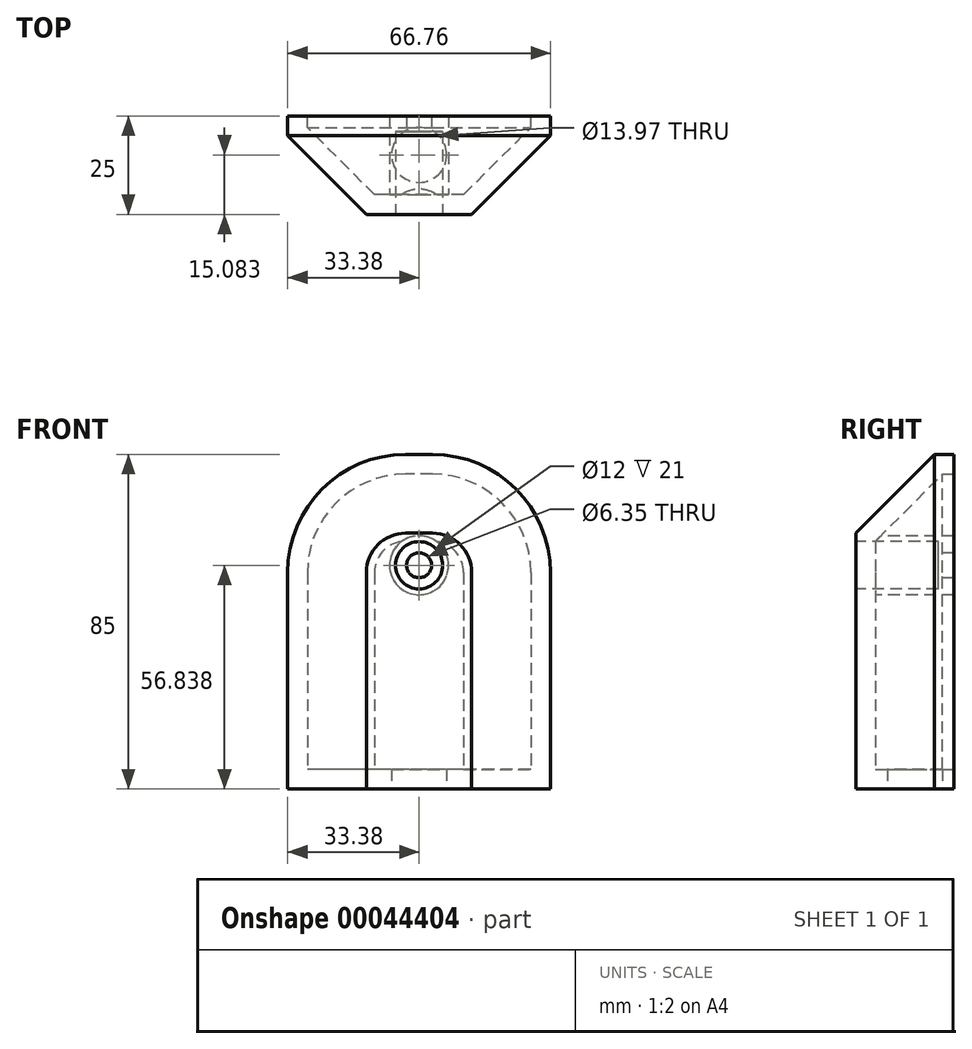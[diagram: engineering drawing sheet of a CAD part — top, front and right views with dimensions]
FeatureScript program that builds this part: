
annotation { "Feature Type Name" : "Feature", "Feature Type Description" : "" }
export const myFeature = defineFeature(function(context is Context, id is Id, definition is map)
    precondition{}
    {
        {
            var Q0;
            Q0=qCreatedBy(makeId("Front.planeOp"),FACE);
            var sketch = newSketch(context, id + "F0", { "sketchPlane" : qUnion([Q0])});
            skLineSegment(sketch, "E0.rect.bottom", {"start": v(3.38, 42.5) * mm, "end": v(-3.38, 42.5) * mm});
            skLineSegment(sketch, "E0.rect.top", {"start": v(33.38, -42.5) * mm, "end": v(-33.38, -42.5) * mm});
            skLineSegment(sketch, "E0.rect.left", {"start": v(33.38, 12.5) * mm, "end": v(33.38, -42.5) * mm});
            skLineSegment(sketch, "E0.rect.right", {"start": v(-33.38, 12.5) * mm, "end": v(-33.38, -42.5) * mm});
            skPoint(sketch, "E0.rect.middle", {"position": v(0, 0) * mm});
            skPoint(sketch, "E1.visualSharp", {"position": v(-33.38, 42.5) * mm});
            skArc(sketch, "E1.filletArc", {"start": v(-3.38, 42.5) * mm, "mid": v(-24.6, 33.71) * mm, "end": v(-33.38, 12.5) * mm});
            skPoint(sketch, "E2.visualSharp", {"position": v(33.38, 42.5) * mm});
            skArc(sketch, "E2.filletArc", {"start": v(33.38, 12.5) * mm, "mid": v(24.6, 33.71) * mm, "end": v(3.38, 42.5) * mm});
            skSolve(sketch);
        }
        {
            var Q0;
            Q0=makeQuery(id+"F0.imprint","IMPRINT",FACE,{"disambiguationData":[TD([[makeQuery(id+"F0.imprint","IMPRINT",EDGE,{"derivedFrom":sQuery(id+"F0.wireOp",EDGE,"E0.rect.bottom")}),1.0]])]});
            extrude(context, id + "F1", {"entities" : qUnion([Q0]), "depth" : 25 * mm});
        }
        {
            var Q0;
            Q0=makeQuery(id+"F1.opExtrude","CAP_EDGE",EDGE,{"disambiguationData":[OSD([sQuery(id+"F0.wireOp",EDGE,"E0.rect.right")])],"isStart":false});
            chamfer(context, id + "F2", {"entities" : qUnion([Q0]), "width" : 20 * mm, "tangentPropagation" : true});
        }
        {
            var Q0;
            Q0=makeQuery(id+"F1.opExtrude","CAP_FACE",FACE,{"disambiguationData":[OSD([sQuery(id+"F0.wireOp",EDGE,"E0.rect.bottom"),sQuery(id+"F0.wireOp",EDGE,"E0.rect.top"),sQuery(id+"F0.wireOp",EDGE,"E0.rect.left"),sQuery(id+"F0.wireOp",EDGE,"E0.rect.right")])],"isStart":true});
            shell(context, id + "F3", {"entities" : qUnion([Q0]), "thickness" : 5 * mm});
        }
        {
            var Q0;
            Q0=makeQuery(id+"F1.opExtrude","SWEPT_FACE",FACE,{"disambiguationData":[OSD([sQuery(id+"F0.wireOp",EDGE,"E0.rect.top")])]});
            var sketch = newSketch(context, id + "F4", { "sketchPlane" : qUnion([Q0])});
            skCircle(sketch, "E3", {"center": v(0, 9.92) * mm, "radius": 6.99 * mm});
            skSolve(sketch);
        }
        {
            var Q0;
            Q0=makeQuery(id+"F4.imprint","IMPRINT",FACE,{"disambiguationData":[TD([[makeQuery(id+"F4.imprint","IMPRINT",EDGE,{"derivedFrom":sQuery(id+"F4.wireOp",EDGE,"E3")}),1.0]])]});
            extrude(context, id + "F5", {"entities" : qUnion([Q0]), "operationType" : NewBodyOperationType.REMOVE, "oppositeDirection" : true, "depth" : 25 * mm});
        }
        {
            var Q0;
            Q0=makeQuery(id+"F1.opExtrude","CAP_FACE",FACE,{"disambiguationData":[OSD([sQuery(id+"F0.wireOp",EDGE,"E0.rect.bottom"),sQuery(id+"F0.wireOp",EDGE,"E0.rect.top"),sQuery(id+"F0.wireOp",EDGE,"E0.rect.left"),sQuery(id+"F0.wireOp",EDGE,"E0.rect.right"),sQuery(id+"F0.wireOp",EDGE,"E1.filletArc"),sQuery(id+"F0.wireOp",EDGE,"E2.filletArc")])],"isStart":false});
            var sketch = newSketch(context, id + "F6", { "sketchPlane" : qUnion([Q0])});
            skCircle(sketch, "E4", {"center": v(0, 14.34) * mm, "radius": 7.5 * mm});
            skSolve(sketch);
        }
        {
            var Q0;
            Q0 = qSketchRegion(id + "F6", true);
            var Q1;
            Q1=qCreatedBy(makeId("Front.planeOp"),FACE);
            extrude(context, id + "F7", {"entities" : qUnion([Q0]), "operationType" : NewBodyOperationType.ADD, "endBound" : BoundingType.UP_TO_SURFACE, "oppositeDirection" : true, "endBoundEntityFace" : qUnion([Q1]), "depth" : 25 * mm});
        }
        {
            var Q0;
            Q0=makeQuery(id+"F6.imprint","IMPRINT",FACE,{"disambiguationData":[TD([[makeQuery(id+"F6.imprint","IMPRINT",EDGE,{"derivedFrom":sQuery(id+"F6.wireOp",EDGE,"E4")}),-1.0]])]});
            var sketch = newSketch(context, id + "F8", { "sketchPlane" : qUnion([Q0])});
            skCircle(sketch, "E5", {"center": v(0, 14.34) * mm, "radius": 6 * mm});
            skSolve(sketch);
        }
        {
            var Q0;
            Q0=qCreatedBy(makeId("Front.planeOp"),FACE);
            cPlane(context, id + "F9", {"entities" : qUnion([Q0]), "cplaneType" : CPlaneType.OFFSET, "offset" : 4 * mm, "width" : 150 * mm, "height" : 150 * mm});
        }
        {
            var Q0;
            Q0 = qSketchRegion(id + "F8", true);
            var Q1;
            Q1=qCreatedBy(id+"F9.planeOp",FACE);
            extrude(context, id + "F10", {"entities" : qUnion([Q0]), "operationType" : NewBodyOperationType.REMOVE, "endBound" : BoundingType.UP_TO_SURFACE, "oppositeDirection" : true, "endBoundEntityFace" : qUnion([Q1]), "depth" : 25 * mm});
        }
        {
            var Q0;
            Q0=makeQuery(id+"F6.imprint","IMPRINT",FACE,{"disambiguationData":[TD([[makeQuery(id+"F6.imprint","IMPRINT",EDGE,{"derivedFrom":sQuery(id+"F6.wireOp",EDGE,"E4")}),-1.0]])]});
            var sketch = newSketch(context, id + "F11", { "sketchPlane" : qUnion([Q0])});
            skCircle(sketch, "E6", {"center": v(0, 14.34) * mm, "radius": 3.18 * mm});
            skSolve(sketch);
        }
        {
            var Q0;
            Q0 = qSketchRegion(id + "F11", true);
            var Q1;
            Q1=qCreatedBy(makeId("Front.planeOp"),FACE);
            extrude(context, id + "F12", {"entities" : qUnion([Q0]), "operationType" : NewBodyOperationType.REMOVE, "endBound" : BoundingType.UP_TO_SURFACE, "oppositeDirection" : true, "endBoundEntityFace" : qUnion([Q1]), "depth" : 25 * mm});
        }
    });
